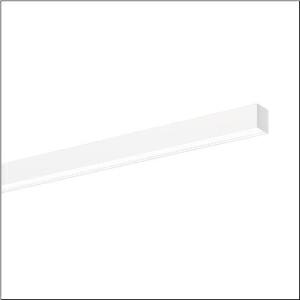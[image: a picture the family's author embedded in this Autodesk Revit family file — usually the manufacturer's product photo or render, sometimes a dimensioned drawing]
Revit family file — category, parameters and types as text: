
# Revit family: silica_r__21_51mx20dc35wb_3ec9
name_source: partatom
category: Lighting Fixtures
units: mm (PartAtom-declared; Revit-internal decimal feet)

## family parameters
Cut with Voids When Loaded = No
Host = Face
Light Source = No
Part Type = Normal
Room Calculation Point = No
Round Connector Dimension = Use Diameter
Shared = No

## types (1)
- --- (1 x LED, 6000 lm, 42.6 W, 3000K)
    Apparent Load = 43 VA
    CIE Flux Codes = 48 79 96 100 100
    Color Rendering = 80
    Color Temperature = 3000K
    Default Elevation = 1800 mm
    Description = Silica® 21, office luminaire, primary optical cover: cover, of PMMA, opal, light emission: direct distribution, primary light characteristic: symmetric, installation type: surface-mounted, LED, rated luminous flux: 6.000lm, luminous efficacy: 141lm/W, light colour: 830, colour temperature: 3000K, with terminal, 3+2-pole, max. 2.5mm², mains connection: 220..240V, AC, 50/60Hz, rated input power: 42.6W, luminaire housing, of aluminium, traffic white (RAL 9016), length: 3.004mm, width: 53mm, height: 53mm, protection rating (complete): IP20, insulation class (complete): insulation class I (protective earthing), certification: CE, permissible operating ambient temperature: 0..+35°C, standard: EN 50419, packaging unit: 1 piece
    Height = 0 mm  [stored 0 ft]
    Lamp = 1 x LED
    Lamp Light Flux = 6000 lm
    Lamp Power = 42.6 W
    Lamp count = 1
    Length = 3004 mm
    Luminous efficacy = 141 lm/W
    Manufacturer = Siteco
    ModVariant = No
    Model = 51MX20DC35WB
    Mounting Place = Ceiling
    Mounting Type = Recessed
    Number of Poles = 1
    OnlyDefault = Yes
    Power Factor = 1
    Product Name = Silica® 21
    Product group = office luminaire | ceiling recessed
    ProductGroupID = 401
    Protection Class = Protection class I
    Protection Degree = IP 20
    RLX_Detail_Level = 1
    RLX_Emergency_Light_Flux = 0 lm
    RLX_Emergency_Type = 0
    RLX_Emergency_Type_DB = No
    RlxData = <blob elided: 23885 chars, md5=4f2cfb73>
    Socket = socket
    Standby Power = 0 W
    System Light Flux = 6000 lm
    System Power = 43 W
    Type Comments = factory setting: luminous flux: 100 % | dim-lin: 254 | 233 mA
    Type Image = l_1297777.jpg
    URL = http://relux.com
    VarID = @adj_048047
    Voltage = 0 V
    Weight = 0.00 kg
    Width = 53 mm

note: [stored X ft] marks values corroborated as IEEE doubles in the binary element streams (Revit-internal decimal feet)

## geometry (parser evidence)
native form markers: Blend x4, Sweep x10
no freeform markers — native parametric forms only
